# Revit family: Horizontal_Roller-PGT-Aluminum-HR710-XOX-Equald
name_source: partatom
category: Windows
revit_build: Autodesk Revit 2015 (Build: 20160512_1515(x64)
units: mm (PartAtom-declared; Revit-internal decimal feet)

## types (1)
- Refer to Type Catalog
    Analytic Construction = <None>
    Assembly Code = B2020110
    BP Calc = 4 1/4"
    BP Calc Center = 4 7/8"
    Color Glass = Glass - PGT - Clear
    Custom Design Note = The types included show default grid/size configurations.  Please reference the 'Product Style Guide' to see all standard configurations and restrictions before creating custom designs.  Please contact PGT Industries with any questions regarding custom designs.
    Default Sill Height = 36"
    Description = Aluminum Horizontal Roller
    Equal Spacing = Yes
    Finish = Metal - PGT - Paint - White
    Grid = Yes
    Grid Layout Note = To edit the grid layout ensure the 'Grid' parameter is turned on and then select an option from the 'Grid Type', 'Grid Type Left' & 'Grid Type Right' drop downs.  Please refer to the 'Product Style Guide' for standard configurations and restrictions.
    Grid Type = Face_Based_Mullion_ 401 : BP
    Grid Type Left = Face_Based_Mullion_ 401 : BP
    Grid Type Right = Face_Based_Mullion_ 401 : BP
    Height = 48"
    Height Calc = 39 11/16"
    Height Calc Center = 40 15/16"
    Manufacturer = PGT Industries
    Maximum Size = 85 1/8” x 63”
    Minimum Size = 52 1/8” x 14 5/8” OR 35 1/4” x 20 7/16”
    Model = HR710
    Product Page URL = http://www.pgtindustries.com
    Product Style Guide = http://www.pgtindustries.com
    Rough Height = 48"
    Rough Width = 90"
    Type Comments = XOX
    URL = http://www.pgtindustries.com
    Wall Closure = By host
    Width = 90"
    Width Calc = 25 1/2"
    Width Calc Center = 25 1/2"

## geometry (parser evidence)
native form markers: Sweep x25
no freeform markers — native parametric forms only
